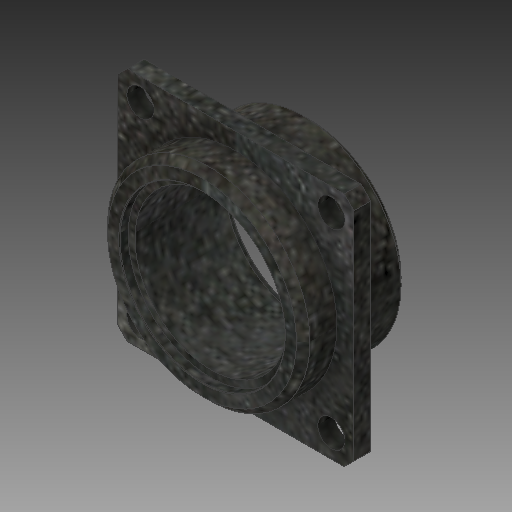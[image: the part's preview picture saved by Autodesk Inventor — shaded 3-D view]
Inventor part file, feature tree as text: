
AUTODESK INVENTOR PART (.ipt)
format: ipt  version: 2018 (Build 220112000, 112)  size: 278,016 bytes
history: native  units: in
note: dims shown in document units (in); Inventor stores cm internally (conversion verified against a paired STEP export)
features: fillet x1
ambient origin geometry x8: Origin, YZ Plane, XZ Plane, XY Plane, X Axis, Y Axis, Z Axis, Center Point
bodies: Solid1 (feature_tree)
feature tree (1):
  fillet  "Fillet2"  [1 undecoded]
note: 1 required parameter value undecoded (feature->parameter linkage not recoverable at this tier; creation-order binding heuristic only, values carry confidence <= 0.55)
